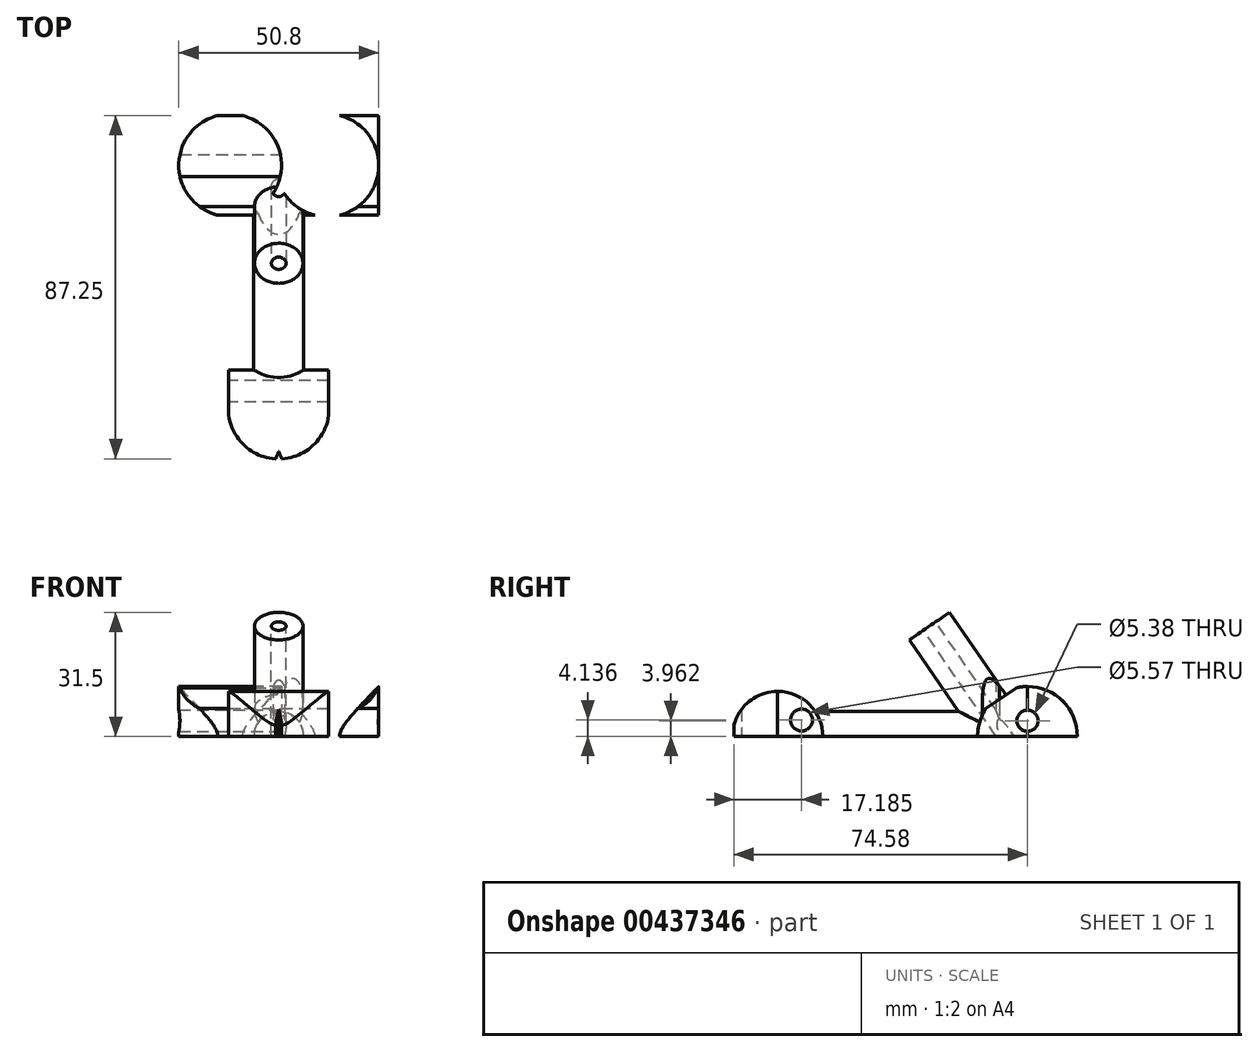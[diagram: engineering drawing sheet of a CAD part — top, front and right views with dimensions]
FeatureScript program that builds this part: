
annotation { "Feature Type Name" : "Feature", "Feature Type Description" : "" }
export const myFeature = defineFeature(function(context is Context, id is Id, definition is map)
    precondition{}
    {
        {
            var Q0;
            Q0=qCreatedBy(makeId("Right.planeOp"),FACE);
            var sketch = newSketch(context, id + "F0", { "sketchPlane" : qUnion([Q0])});
            skCircle(sketch, "E0", {"center": v(0, 0) * mm, "radius": 12.67 * mm});
            skSolve(sketch);
        }
        {
            var Q0;
            Q0 = qSketchRegion(id + "F0", true);
            extrude(context, id + "F1", {"entities" : qUnion([Q0]), "depth" : 50.8 * mm});
        }
        {
            var Q0;
            Q0=makeQuery(id+"F1.opExtrude","CAP_FACE",FACE,{"disambiguationData":[OSD([sQuery(id+"F0.wireOp",EDGE,"E0")])],"isStart":true});
            var sketch = newSketch(context, id + "F2", { "sketchPlane" : qUnion([Q0])});
            skLineSegment(sketch, "E1", {"start": v(-12.67, 0) * mm, "end": v(12.67, 0) * mm});
            skLineSegment(sketch, "E2", {"start": v(12.67, 0) * mm, "end": v(16.57, -18.44) * mm});
            skLineSegment(sketch, "E3", {"start": v(16.57, -18.44) * mm, "end": v(-14.68, -18.44) * mm});
            skLineSegment(sketch, "E4", {"start": v(-14.68, -18.44) * mm, "end": v(-12.67, 0) * mm});
            skSolve(sketch);
        }
        {
            var Q0;
            Q0 = qSketchRegion(id + "F2", true);
            extrude(context, id + "F3", {"entities" : qUnion([Q0]), "operationType" : NewBodyOperationType.REMOVE, "oppositeDirection" : true, "depth" : 50.8 * mm});
        }
        {
            var Q0;
            Q0=makeQuery(id+"F1.opExtrude","CAP_FACE",FACE,{"disambiguationData":[OSD([sQuery(id+"F0.wireOp",EDGE,"E0")])],"isStart":true});
            extrude(context, id + "F4", {"entities" : qUnion([Q0]), "operationType" : NewBodyOperationType.ADD, "depth" : 50.8 * mm});
        }
        {
            var Q0;
            Q0=makeQuery(id+"F4.opExtrude","CAP_FACE",FACE,{"disambiguationData":[OSD([sQuery(id+"F0.wireOp",EDGE,"E0")])],"isStart":false});
            extrude(context, id + "F5", {"entities" : qUnion([Q0]), "operationType" : NewBodyOperationType.REMOVE, "oppositeDirection" : true, "depth" : 25.4 * mm});
        }
        {
            var Q0;
            Q0=makeQuery(id+"F1.opExtrude","CAP_FACE",FACE,{"disambiguationData":[OSD([sQuery(id+"F0.wireOp",EDGE,"E0")])],"isStart":false});
            extrude(context, id + "F6", {"entities" : qUnion([Q0]), "operationType" : NewBodyOperationType.REMOVE, "oppositeDirection" : true, "depth" : 25.4 * mm});
        }
        {
            var Q0;
            Q0=qCreatedBy(makeId("Front.planeOp"),FACE);
            var sketch = newSketch(context, id + "F7", { "sketchPlane" : qUnion([Q0])});
            skCircle(sketch, "E5", {"center": v(0, 0) * mm, "radius": 6.34 * mm});
            skSolve(sketch);
        }
        {
            var Q0;
            Q0 = qSketchRegion(id + "F7", true);
            extrude(context, id + "F8", {"entities" : qUnion([Q0]), "operationType" : NewBodyOperationType.ADD, "depth" : 101.6 * mm});
        }
        {
            var Q0;
            Q0=makeQuery(id+"F8.opExtrude","CAP_FACE",FACE,{"disambiguationData":[OSD([sQuery(id+"F7.wireOp",EDGE,"E5")])],"isStart":false});
            var sketch = newSketch(context, id + "F9", { "sketchPlane" : qUnion([Q0])});
            skLineSegment(sketch, "E6", {"start": v(-10.43, 0) * mm, "end": v(11.6, 0) * mm});
            skLineSegment(sketch, "E7", {"start": v(11.6, 0) * mm, "end": v(11.6, -12.4) * mm});
            skLineSegment(sketch, "E8", {"start": v(11.6, -12.4) * mm, "end": v(-10.43, -12.4) * mm});
            skLineSegment(sketch, "E9", {"start": v(-10.43, -12.4) * mm, "end": v(-10.43, 0) * mm});
            skSolve(sketch);
        }
        {
            var Q0;
            Q0 = qSketchRegion(id + "F9", true);
            extrude(context, id + "F10", {"entities" : qUnion([Q0]), "operationType" : NewBodyOperationType.REMOVE, "oppositeDirection" : true, "depth" : 101.6 * mm});
        }
        {
            var Q0;
            Q0=makeQuery(id+"F6.boolean.opBoolean","COPY",FACE,{"derivedFrom":makeQuery(id+"F6.opExtrude","CAP_FACE",FACE,{"disambiguationData":[OSD([sQuery(id+"F0.wireOp",EDGE,"E0")])],"isStart":false})});
            var sketch = newSketch(context, id + "F11", { "sketchPlane" : qUnion([Q0])});
            skCircle(sketch, "E10", {"center": v(0, 3.96) * mm, "radius": 2.7 * mm});
            skSolve(sketch);
        }
        {
            var Q0;
            Q0 = qSketchRegion(id + "F11", true);
            extrude(context, id + "F12", {"entities" : qUnion([Q0]), "operationType" : NewBodyOperationType.REMOVE, "oppositeDirection" : true, "depth" : 76.2 * mm});
        }
        {
            var Q0;
            Q0=makeQuery(id+"F6.boolean.opBoolean","COPY",FACE,{"derivedFrom":makeQuery(id+"F6.opExtrude","CAP_FACE",FACE,{"disambiguationData":[OSD([sQuery(id+"F0.wireOp",EDGE,"E0")])],"isStart":false})});
            var sketch = newSketch(context, id + "F13", { "sketchPlane" : qUnion([Q0])});
            skLineSegment(sketch, "E11", {"start": v(-10.51, 7.06) * mm, "end": v(-2.81, 12.35) * mm});
            skLineSegment(sketch, "E12", {"start": v(-2.81, 12.35) * mm, "end": v(-2.81, 21.62) * mm});
            skLineSegment(sketch, "E13", {"start": v(-2.81, 21.62) * mm, "end": v(-12.67, 11.7) * mm});
            skLineSegment(sketch, "E14", {"start": v(-12.67, 11.7) * mm, "end": v(-10.51, 7.06) * mm});
            skSolve(sketch);
        }
        {
            var Q0;
            Q0 = qSketchRegion(id + "F13", true);
            extrude(context, id + "F14", {"entities" : qUnion([Q0]), "operationType" : NewBodyOperationType.REMOVE, "oppositeDirection" : true, "depth" : 101.6 * mm});
        }
        {
            var Q0;
            Q0=makeQuery(id+"F14.boolean.opBoolean","COPY",FACE,{"derivedFrom":makeQuery(id+"F14.opExtrude","SWEPT_FACE",FACE,{"disambiguationData":[OSD([sQuery(id+"F13.wireOp",EDGE,"E11")])]})});
            var sketch = newSketch(context, id + "F15", { "sketchPlane" : qUnion([Q0])});
            skCircle(sketch, "E15", {"center": v(0, -4.67) * mm, "radius": 6.17 * mm});
            skSolve(sketch);
        }
        {
            var Q0;
            Q0 = qSketchRegion(id + "F15", true);
            extrude(context, id + "F16", {"entities" : qUnion([Q0]), "operationType" : NewBodyOperationType.ADD, "depth" : 25.4 * mm});
        }
        {
            var Q0;
            Q0=makeQuery(id+"F16.opExtrude","CAP_FACE",FACE,{"disambiguationData":[OSD([sQuery(id+"F15.wireOp",EDGE,"E15")])],"isStart":true});
            extrude(context, id + "F17", {"entities" : qUnion([Q0]), "operationType" : NewBodyOperationType.ADD, "depth" : 5.08 * mm});
        }
        {
            var Q0;
            Q0=makeQuery(id+"F16.opExtrude","CAP_FACE",FACE,{"disambiguationData":[OSD([sQuery(id+"F15.wireOp",EDGE,"E15")])],"isStart":false});
            var sketch = newSketch(context, id + "F18", { "sketchPlane" : qUnion([Q0])});
            skCircle(sketch, "E16", {"center": v(0, -4.67) * mm, "radius": 1.88 * mm});
            skSolve(sketch);
        }
        {
            var Q0;
            Q0 = qSketchRegion(id + "F18", true);
            extrude(context, id + "F19", {"entities" : qUnion([Q0]), "operationType" : NewBodyOperationType.REMOVE, "oppositeDirection" : true, "depth" : 127 * mm});
        }
        {
            var Q0;
            {var subQ0=sQuery(id+"F2.wireOp",EDGE,"E1");Q0=makeQuery(id+"FZ7nRMHTZIAHilV_1.boolean.opBoolean","MERGE",FACE,{"derivedFrom":[makeQuery(id+"F10.boolean.opBoolean","MERGE",FACE,{"derivedFrom":[makeQuery(id+"F4.boolean.opBoolean","MERGE",FACE,{"derivedFrom":[makeQuery(id+"F3.boolean.opBoolean","COPY",FACE,{"derivedFrom":makeQuery(id+"F3.opExtrude","SWEPT_FACE",FACE,{"disambiguationData":[OSD([subQ0])]})}),makeQuery(id+"F4.opExtrude","SWEPT_FACE",FACE,{"disambiguationData":[OSD([subQ0])]})]}),makeQuery(id+"F10.opExtrude","SWEPT_FACE",FACE,{"disambiguationData":[OSD([sQuery(id+"F9.wireOp",EDGE,"E6")])]})]}),makeQuery(id+"FZ7nRMHTZIAHilV_1.opExtrude","SWEPT_FACE",FACE,{"disambiguationData":[OSD([sQuery(id+"FZHSD0famrwk4mK_1.wireOp",EDGE,"AMHjZNhX-U3ob-k1hZ-kngq-pmHeKkSt02t4")])]})]});}
            var sketch = newSketch(context, id + "F20", { "sketchPlane" : qUnion([Q0])});
            skLineSegment(sketch, "E17", {"start": v(0, 107.44) * mm, "end": v(-1.27, 114.22) * mm});
            skLineSegment(sketch, "E18", {"start": v(-1.27, 114.22) * mm, "end": v(1.26, 114.22) * mm});
            skLineSegment(sketch, "E19", {"start": v(1.26, 114.22) * mm, "end": v(0, 107.44) * mm});
            skSolve(sketch);
        }
        {
            var Q0;
            Q0 = qSketchRegion(id + "F20", true);
            extrude(context, id + "F21", {"entities" : qUnion([Q0]), "operationType" : NewBodyOperationType.REMOVE, "oppositeDirection" : true, "depth" : 25.4 * mm});
        }
        {
            var Q0;
            {var subQ0=sQuery(id+"F2.wireOp",EDGE,"E1");Q0=makeQuery(id+"FZ7nRMHTZIAHilV_1.boolean.opBoolean","MERGE",FACE,{"derivedFrom":[makeQuery(id+"F10.boolean.opBoolean","MERGE",FACE,{"derivedFrom":[makeQuery(id+"F4.boolean.opBoolean","MERGE",FACE,{"derivedFrom":[makeQuery(id+"F3.boolean.opBoolean","COPY",FACE,{"derivedFrom":makeQuery(id+"F3.opExtrude","SWEPT_FACE",FACE,{"disambiguationData":[OSD([subQ0])]})}),makeQuery(id+"F4.opExtrude","SWEPT_FACE",FACE,{"disambiguationData":[OSD([subQ0])]})]}),makeQuery(id+"F10.opExtrude","SWEPT_FACE",FACE,{"disambiguationData":[OSD([sQuery(id+"F9.wireOp",EDGE,"E6")])]})]}),makeQuery(id+"FZ7nRMHTZIAHilV_1.opExtrude","SWEPT_FACE",FACE,{"disambiguationData":[OSD([sQuery(id+"FZHSD0famrwk4mK_1.wireOp",EDGE,"AMHjZNhX-U3ob-k1hZ-kngq-pmHeKkSt02t4")])]})]});}
            var sketch = newSketch(context, id + "F22", { "sketchPlane" : qUnion([Q0])});
            skCircle(sketch, "E20", {"center": v(-12.35, 0) * mm, "radius": 13.05 * mm});
            skCircle(sketch, "E21.MirrorC", {"center": v(12.35, 0) * mm, "radius": 13.05 * mm});
            skSolve(sketch);
        }
        {
            var Q0;
            {var subQ0=sQuery(id+"F22.wireOp",EDGE,"E20");var subQ2=sQuery(id+"F2.wireOp",EDGE,"E1");var subQ6=makeQuery(id+"F5.boolean.opBoolean","COPY",EDGE,{"derivedFrom":makeQuery(id+"F5.opExtrude","CAP_EDGE",EDGE,{"disambiguationData":[OSD([subQ2])],"isStart":false})});var subQ7=makeQuery(id+"F22.imprint","INTERSECT",VERTEX,{"derivedFrom":[subQ6,subQ0]});Q0=makeQuery(id+"F22.imprint","IMPRINT",FACE,{"disambiguationData":[TD([[makeQuery(id+"F22.imprint","IMPRINT",EDGE,{"disambiguationData":[TD([[subQ7,1.0]])],"derivedFrom":subQ0}),-1.0]])]});}
            var Q1;
            {var subQ0=sQuery(id+"F22.wireOp",EDGE,"E20");var subQ1=sQuery(id+"F2.wireOp",EDGE,"E1");var subQ2=makeQuery(id+"F5.boolean.opBoolean","COPY",EDGE,{"derivedFrom":makeQuery(id+"F5.opExtrude","CAP_EDGE",EDGE,{"disambiguationData":[OSD([subQ1])],"isStart":false})});var subQ3=makeQuery(id+"F22.imprint","INTERSECT",VERTEX,{"derivedFrom":[subQ2,subQ0]});Q1=makeQuery(id+"F22.imprint","IMPRINT",FACE,{"disambiguationData":[TD([[makeQuery(id+"F22.imprint","IMPRINT",EDGE,{"disambiguationData":[TD([[subQ3,-1.0]])],"derivedFrom":subQ0}),-1.0]])]});}
            var Q2;
            {var subQ0=sQuery(id+"F22.wireOp",EDGE,"E21.MirrorC");var subQ1=sQuery(id+"F22.wireOp",EDGE,"E20");var subQ2=makeQuery(id+"F22.imprint","INTERSECT",VERTEX,{"disambiguationData":[OD(1.0)],"derivedFrom":[subQ1,subQ0]});Q2=makeQuery(id+"F22.imprint","IMPRINT",FACE,{"disambiguationData":[TD([[makeQuery(id+"F22.imprint","IMPRINT",EDGE,{"disambiguationData":[TD([[subQ2,1.0]])],"derivedFrom":subQ1}),-1.0]])]});}
            var Q3;
            {var subQ0=sQuery(id+"F22.wireOp",EDGE,"E21.MirrorC");var subQ1=sQuery(id+"F2.wireOp",EDGE,"E1");var subQ2=makeQuery(id+"F6.boolean.opBoolean","COPY",EDGE,{"derivedFrom":makeQuery(id+"F6.opExtrude","CAP_EDGE",EDGE,{"disambiguationData":[OSD([subQ1])],"isStart":false})});var subQ3=makeQuery(id+"F22.imprint","INTERSECT",VERTEX,{"derivedFrom":[subQ2,subQ0]});Q3=makeQuery(id+"F22.imprint","IMPRINT",FACE,{"disambiguationData":[TD([[makeQuery(id+"F22.imprint","IMPRINT",EDGE,{"disambiguationData":[TD([[subQ3,-1.0]])],"derivedFrom":subQ0}),1.0]])]});}
            var Q4;
            {var subQ0=sQuery(id+"F22.wireOp",EDGE,"E21.MirrorC");var subQ2=sQuery(id+"F2.wireOp",EDGE,"E1");var subQ6=makeQuery(id+"F6.boolean.opBoolean","COPY",EDGE,{"derivedFrom":makeQuery(id+"F6.opExtrude","CAP_EDGE",EDGE,{"disambiguationData":[OSD([subQ2])],"isStart":false})});var subQ7=makeQuery(id+"F22.imprint","INTERSECT",VERTEX,{"derivedFrom":[subQ6,subQ0]});Q4=makeQuery(id+"F22.imprint","IMPRINT",FACE,{"disambiguationData":[TD([[makeQuery(id+"F22.imprint","IMPRINT",EDGE,{"disambiguationData":[TD([[subQ7,1.0]])],"derivedFrom":subQ0}),1.0]])]});}
            extrude(context, id + "F23", {"entities" : qUnion([Q0, Q1, Q2, Q3, Q4]), "operationType" : NewBodyOperationType.REMOVE, "oppositeDirection" : true, "depth" : 50.8 * mm});
        }
        {
            var Q0;
            Q0=makeQuery(id+"F8.opExtrude","CAP_FACE",FACE,{"disambiguationData":[OSD([sQuery(id+"F7.wireOp",EDGE,"E5")])],"isStart":false});
            extrude(context, id + "F24", {"entities" : qUnion([Q0]), "operationType" : NewBodyOperationType.REMOVE, "oppositeDirection" : true, "depth" : 38.1 * mm});
        }
        {
            var Q0;
            Q0=qCreatedBy(makeId("Right.planeOp"),FACE);
            var sketch = newSketch(context, id + "F25", { "sketchPlane" : qUnion([Q0])});
            skCircle(sketch, "E22", {"center": v(-63.46, 0) * mm, "radius": 11.45 * mm});
            skSolve(sketch);
        }
        {
            var Q0;
            Q0 = qSketchRegion(id + "F25", true);
            extrude(context, id + "F26", {"entities" : qUnion([Q0]), "operationType" : NewBodyOperationType.ADD, "depth" : 12.7 * mm});
        }
        {
            var Q0;
            Q0=makeQuery(id+"F26.opExtrude","CAP_FACE",FACE,{"disambiguationData":[OSD([sQuery(id+"F25.wireOp",EDGE,"E22")])],"isStart":true});
            var sketch = newSketch(context, id + "F27", { "sketchPlane" : qUnion([Q0])});
            skCircle(sketch, "E23", {"center": v(63.46, 0) * mm, "radius": 11.45 * mm});
            skPoint(sketch, "E23.first.point", {"position": v(55.77, -8.48) * mm});
            skPoint(sketch, "E23.second.point", {"position": v(71.1, 8.54) * mm});
            skPoint(sketch, "E23.third.point", {"position": v(55.2, 7.93) * mm});
            skSolve(sketch);
        }
        {
            var Q0;
            Q0 = qSketchRegion(id + "F27", true);
            extrude(context, id + "F28", {"entities" : qUnion([Q0]), "operationType" : NewBodyOperationType.ADD, "depth" : 12.7 * mm});
        }
        {
            var Q0;
            Q0=makeQuery(id+"F26.opExtrude","CAP_FACE",FACE,{"disambiguationData":[OSD([sQuery(id+"F25.wireOp",EDGE,"E22")])],"isStart":false});
            var sketch = newSketch(context, id + "F29", { "sketchPlane" : qUnion([Q0])});
            skLineSegment(sketch, "E24", {"start": v(-74.91, 0) * mm, "end": v(-77.6, -17.66) * mm});
            skLineSegment(sketch, "E25", {"start": v(-77.6, -17.66) * mm, "end": v(-49.87, -17.66) * mm});
            skLineSegment(sketch, "E26", {"start": v(-49.87, -17.66) * mm, "end": v(-51.94, 0) * mm});
            skLineSegment(sketch, "E27", {"start": v(-51.94, 0) * mm, "end": v(-74.91, 0) * mm});
            skSolve(sketch);
        }
        {
            var Q0;
            Q0 = qSketchRegion(id + "F29", true);
            extrude(context, id + "F30", {"entities" : qUnion([Q0]), "operationType" : NewBodyOperationType.REMOVE, "oppositeDirection" : true, "depth" : 25.4 * mm});
        }
        {
            var Q0;
            {var subQ0=sQuery(id+"F2.wireOp",EDGE,"E1");Q0=makeQuery(id+"F30.boolean.opBoolean","MERGE",FACE,{"derivedFrom":[makeQuery(id+"F10.boolean.opBoolean","MERGE",FACE,{"derivedFrom":[makeQuery(id+"F4.boolean.opBoolean","MERGE",FACE,{"derivedFrom":[makeQuery(id+"F3.boolean.opBoolean","COPY",FACE,{"derivedFrom":makeQuery(id+"F3.opExtrude","SWEPT_FACE",FACE,{"disambiguationData":[OSD([subQ0])]})}),makeQuery(id+"F4.opExtrude","SWEPT_FACE",FACE,{"disambiguationData":[OSD([subQ0])]})]}),makeQuery(id+"F10.opExtrude","SWEPT_FACE",FACE,{"disambiguationData":[OSD([sQuery(id+"F9.wireOp",EDGE,"E6")])]})]}),makeQuery(id+"F30.opExtrude","SWEPT_FACE",FACE,{"disambiguationData":[OSD([sQuery(id+"F29.wireOp",EDGE,"E27")])]})]});}
            var sketch = newSketch(context, id + "F31", { "sketchPlane" : qUnion([Q0])});
            skArc(sketch, "E28", {"start": v(12.7, 63.46) * mm, "mid": v(0, 74.6) * mm, "end": v(-12.7, 63.46) * mm});
            skSolve(sketch);
        }
        {
            var Q0;
            {var subQ0=sQuery(id+"F31.wireOp",EDGE,"E28");Q0=makeQuery(id+"F31.imprint","IMPRINT",FACE,{"disambiguationData":[TD([[makeQuery(id+"F31.imprint","IMPRINT",EDGE,{"derivedFrom":subQ0}),-1.0]])]});}
            extrude(context, id + "F32", {"entities" : qUnion([Q0]), "operationType" : NewBodyOperationType.REMOVE, "oppositeDirection" : true, "depth" : 25.4 * mm});
        }
        {
            var Q0;
            {var subQ0=sQuery(id+"F2.wireOp",EDGE,"E1");Q0=makeQuery(id+"F30.boolean.opBoolean","MERGE",FACE,{"derivedFrom":[makeQuery(id+"F10.boolean.opBoolean","MERGE",FACE,{"derivedFrom":[makeQuery(id+"F4.boolean.opBoolean","MERGE",FACE,{"derivedFrom":[makeQuery(id+"F3.boolean.opBoolean","COPY",FACE,{"derivedFrom":makeQuery(id+"F3.opExtrude","SWEPT_FACE",FACE,{"disambiguationData":[OSD([subQ0])]})}),makeQuery(id+"F4.opExtrude","SWEPT_FACE",FACE,{"disambiguationData":[OSD([subQ0])]})]}),makeQuery(id+"F10.opExtrude","SWEPT_FACE",FACE,{"disambiguationData":[OSD([sQuery(id+"F9.wireOp",EDGE,"E6")])]})]}),makeQuery(id+"F30.opExtrude","SWEPT_FACE",FACE,{"disambiguationData":[OSD([sQuery(id+"F29.wireOp",EDGE,"E27")])]})]});}
            var sketch = newSketch(context, id + "F33", { "sketchPlane" : qUnion([Q0])});
            skLineSegment(sketch, "E29", {"start": v(0, 74.6) * mm, "end": v(-0.8, 74.6) * mm});
            skLineSegment(sketch, "E30", {"start": v(-0.8, 74.6) * mm, "end": v(0, 72.65) * mm});
            skLineSegment(sketch, "E31", {"start": v(0, 74.6) * mm, "end": v(0.79, 74.6) * mm});
            skLineSegment(sketch, "E32", {"start": v(0.79, 74.6) * mm, "end": v(0, 72.65) * mm});
            skSolve(sketch);
        }
        {
            var Q0;
            Q0 = qSketchRegion(id + "F33", true);
            extrude(context, id + "F34", {"entities" : qUnion([Q0]), "operationType" : NewBodyOperationType.REMOVE, "oppositeDirection" : true, "depth" : 25.4 * mm});
        }
        {
            var Q0;
            Q0=makeQuery(id+"F28.opExtrude","CAP_FACE",FACE,{"disambiguationData":[OSD([sQuery(id+"F27.wireOp",EDGE,"E23")])],"isStart":false});
            var sketch = newSketch(context, id + "F35", { "sketchPlane" : qUnion([Q0])});
            skCircle(sketch, "E33", {"center": v(57.4, 4.14) * mm, "radius": 2.79 * mm});
            skSolve(sketch);
        }
        {
            var Q0;
            Q0 = qSketchRegion(id + "F35", true);
            extrude(context, id + "F36", {"entities" : qUnion([Q0]), "operationType" : NewBodyOperationType.REMOVE, "oppositeDirection" : true, "depth" : 25.4 * mm});
        }
    });
